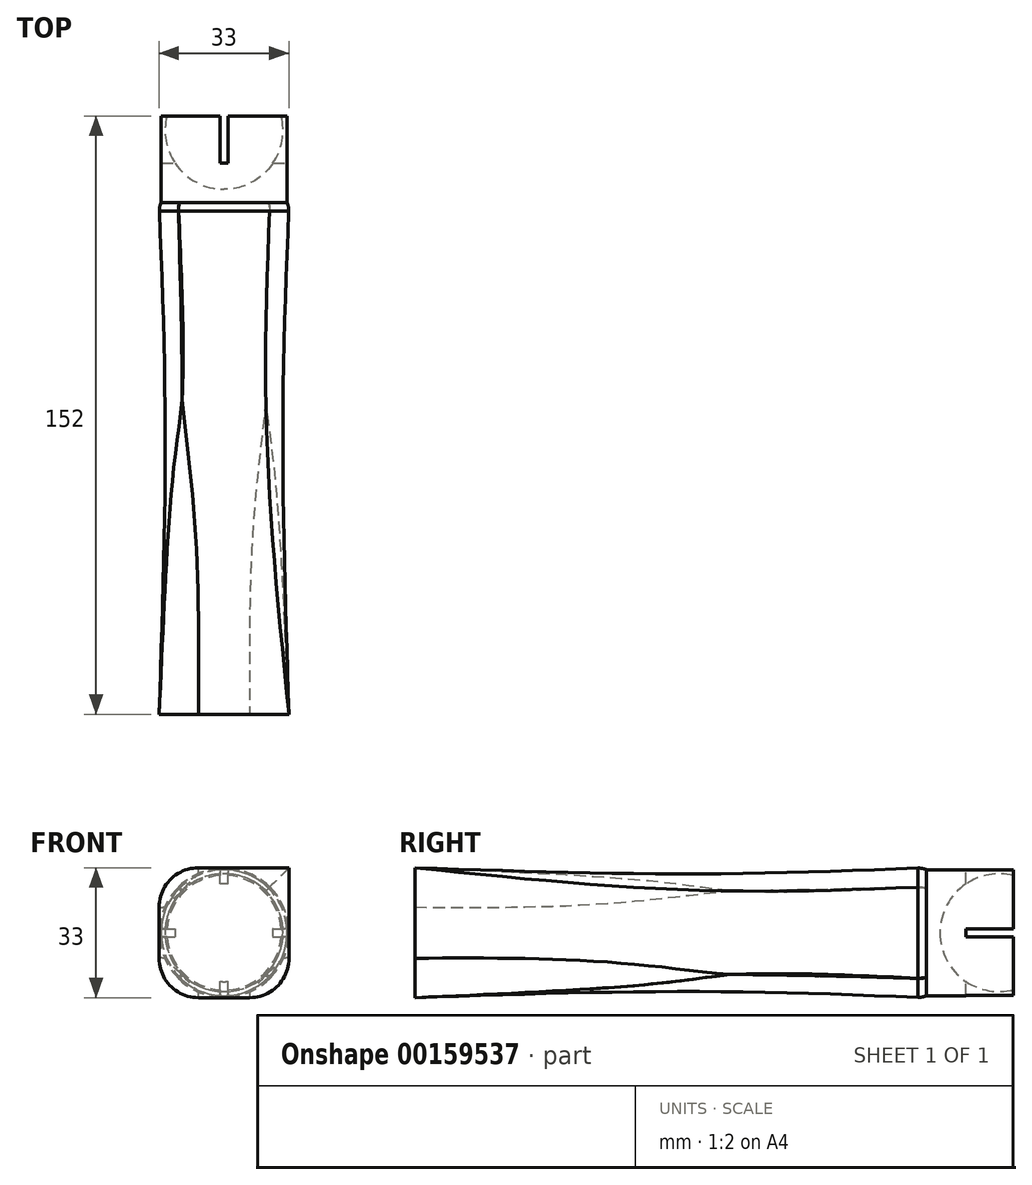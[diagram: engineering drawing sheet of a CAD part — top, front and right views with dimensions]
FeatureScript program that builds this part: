
annotation { "Feature Type Name" : "Feature", "Feature Type Description" : "" }
export const myFeature = defineFeature(function(context is Context, id is Id, definition is map)
    precondition{}
    {
        {
            var Q0;
            Q0=qCreatedBy(makeId("Front.planeOp"),FACE);
            cPlane(context, id + "F0", {"entities" : qUnion([Q0]), "cplaneType" : CPlaneType.OFFSET, "offset" : 70 * mm, "width" : 152.4 * mm, "height" : 152.4 * mm});
        }
        {
            var Q0;
            Q0=qCreatedBy(makeId("Front.planeOp"),FACE);
            cPlane(context, id + "F1", {"entities" : qUnion([Q0]), "cplaneType" : CPlaneType.OFFSET, "offset" : 10 * mm, "oppositeDirection" : true, "width" : 152.4 * mm, "height" : 152.4 * mm});
        }
        {
            var Q0;
            Q0=qCreatedBy(id+"F0.planeOp",FACE);
            var sketch = newSketch(context, id + "F2", { "sketchPlane" : qUnion([Q0])});
            skLineSegment(sketch, "E0.bottom", {"start": v(-16.5, 16.5) * mm, "end": v(16.5, 16.5) * mm});
            skLineSegment(sketch, "E0.top", {"start": v(-16.5, -16.5) * mm, "end": v(16.5, -16.5) * mm});
            skLineSegment(sketch, "E0.left", {"start": v(-16.5, 16.5) * mm, "end": v(-16.5, -16.5) * mm});
            skLineSegment(sketch, "E0.right", {"start": v(16.5, 16.5) * mm, "end": v(16.5, -16.5) * mm});
            skPoint(sketch, "E0.middle", {"position": v(0, 0) * mm});
            skSolve(sketch);
        }
        {
            var Q0;
            Q0=qCreatedBy(id+"F1.planeOp",FACE);
            var sketch = newSketch(context, id + "F3", { "sketchPlane" : qUnion([Q0])});
            skCircle(sketch, "E1", {"center": v(0, 0) * mm, "radius": 15 * mm});
            skSolve(sketch);
        }
        {
            var Q0;
            Q0=qCreatedBy(id+"F1.planeOp",FACE);
            cPlane(context, id + "F4", {"entities" : qUnion([Q0]), "cplaneType" : CPlaneType.OFFSET, "offset" : 50 * mm, "oppositeDirection" : true, "width" : 150 * mm, "height" : 150 * mm});
        }
        {
            var Q0;
            Q0=qCreatedBy(id+"F4.planeOp",FACE);
            var sketch = newSketch(context, id + "F5", { "sketchPlane" : qUnion([Q0])});
            skCircle(sketch, "E2", {"center": v(0, 0) * mm, "radius": 16.5 * mm});
            skSolve(sketch);
        }
        {
            var Q0;
            Q0=makeQuery(id+"F2.imprint","IMPRINT",FACE,{"disambiguationData":[TD([[makeQuery(id+"F2.imprint","IMPRINT",EDGE,{"derivedFrom":sQuery(id+"F2.wireOp",EDGE,"E0.bottom")}),-1.0]])]});
            var Q1;
            Q1=makeQuery(id+"F3.imprint","IMPRINT",FACE,{"disambiguationData":[TD([[makeQuery(id+"F3.imprint","IMPRINT",EDGE,{"derivedFrom":sQuery(id+"F3.wireOp",EDGE,"E1")}),1.0]])]});
            var Q2;
            Q2=makeQuery(id+"F5.imprint","IMPRINT",FACE,{"disambiguationData":[TD([[makeQuery(id+"F5.imprint","IMPRINT",EDGE,{"derivedFrom":sQuery(id+"F5.wireOp",EDGE,"E2")}),1.0]])]});
            loft(context, id + "F6", {"sheetProfilesArray" : [{ "sheetProfileEntities" : qUnion([Q0]) }, { "sheetProfileEntities" : qUnion([Q1]) }, { "sheetProfileEntities" : qUnion([Q2]) }]});
        }
        {
            var Q0;
            Q0=makeQuery(id+"F6.opLoft","SWEPT_EDGE",EDGE,{"disambiguationData":[OSD([sQuery(id+"F2.wireOp",EDGE,"E0.bottom"),sQuery(id+"F2.wireOp",EDGE,"E0.left")]),OD(0.0)]});
            var Q1;
            Q1=makeQuery(id+"F6.opLoft","SWEPT_EDGE",EDGE,{"disambiguationData":[OSD([sQuery(id+"F2.wireOp",EDGE,"E0.bottom"),sQuery(id+"F2.wireOp",EDGE,"E0.left"),sQuery(id+"F2.wireOp",EDGE,"E0.right"),sQuery(id+"F3.wireOp",EDGE,"E1")])]});
            var Q2;
            Q2=makeQuery(id+"F6.opLoft","SWEPT_EDGE",EDGE,{"disambiguationData":[OSD([sQuery(id+"F2.wireOp",EDGE,"E0.top"),sQuery(id+"F2.wireOp",EDGE,"E0.left"),sQuery(id+"F2.wireOp",EDGE,"E0.right"),sQuery(id+"F3.wireOp",EDGE,"E1")])]});
            var Q3;
            Q3=makeQuery(id+"F6.opLoft","SWEPT_EDGE",EDGE,{"disambiguationData":[OSD([sQuery(id+"F2.wireOp",EDGE,"E0.bottom"),sQuery(id+"F2.wireOp",EDGE,"E0.top"),sQuery(id+"F2.wireOp",EDGE,"E0.right"),sQuery(id+"F3.wireOp",EDGE,"E1")])]});
            fillet(context, id + "F7", {"entities" : qUnion([Q0, Q1, Q2, Q3]), "radius" : 10 * mm, "tangentPropagation" : true, "allowEdgeOverflow" : false});
        }
        {
            var Q0;
            Q0=makeQuery(id+"F5.imprint","IMPRINT",FACE,{"disambiguationData":[TD([[makeQuery(id+"F5.imprint","IMPRINT",EDGE,{"derivedFrom":sQuery(id+"F5.wireOp",EDGE,"E2")}),1.0]])]});
            var sketch = newSketch(context, id + "F8", { "sketchPlane" : qUnion([Q0])});
            skCircle(sketch, "E3", {"center": v(0, 0) * mm, "radius": 16 * mm});
            skSolve(sketch);
        }
        {
            var Q0;
            Q0 = qSketchRegion(id + "F8", true);
            extrude(context, id + "F9", {"entities" : qUnion([Q0]), "operationType" : NewBodyOperationType.ADD, "oppositeDirection" : true, "depth" : 22 * mm});
        }
        {
            var Q0;
            Q0=qCreatedBy(makeId("Top.planeOp"),FACE);
            var sketch = newSketch(context, id + "F10", { "sketchPlane" : qUnion([Q0])});
            skArc(sketch, "E4", {"start": v(0, 63.4) * mm, "mid": v(15, 78.4) * mm, "end": v(0, 93.4) * mm});
            skLineSegment(sketch, "E5", {"start": v(0, 224.37) * mm, "end": v(0, 31.68) * mm});
            skSolve(sketch);
        }
        {
            var Q0;
            Q0 = qSketchRegion(id + "F10", true);
            var Q1;
            Q1=sQuery(id+"F10.wireOp",EDGE,"E5");
            revolve(context, id + "F11", {"operationType" : NewBodyOperationType.REMOVE, "entities" : qUnion([Q0]), "axis" : qUnion([Q1]), "revolveType" : RevolveType.FULL, "oppositeDirection" : true});
        }
        {
            var Q0;
            Q0=qCreatedBy(makeId("Top.planeOp"),FACE);
            var sketch = newSketch(context, id + "F12", { "sketchPlane" : qUnion([Q0])});
            skLineSegment(sketch, "E6.bottom", {"start": v(-1, 90) * mm, "end": v(1, 90) * mm});
            skLineSegment(sketch, "E6.top", {"start": v(-1, 70) * mm, "end": v(1, 70) * mm});
            skLineSegment(sketch, "E6.left", {"start": v(-1, 90) * mm, "end": v(-1, 70) * mm});
            skLineSegment(sketch, "E6.right", {"start": v(1, 90) * mm, "end": v(1, 70) * mm});
            skPoint(sketch, "E6.middle", {"position": v(0, 80) * mm});
            skSolve(sketch);
        }
        {
            var Q0;
            Q0 = qSketchRegion(id + "F12", true);
            extrude(context, id + "F13", {"entities" : qUnion([Q0]), "operationType" : NewBodyOperationType.REMOVE, "endBound" : BoundingType.SYMMETRIC, "oppositeDirection" : true, "depth" : 25 * mm});
        }
        {
            var Q0;
            Q0=qCreatedBy(makeId("Right.planeOp"),FACE);
            var sketch = newSketch(context, id + "F14", { "sketchPlane" : qUnion([Q0])});
            skPoint(sketch, "E7.middle", {"position": v(37.45, 0) * mm});
            skLineSegment(sketch, "E8.bottom", {"start": v(90, 1) * mm, "end": v(70, 1) * mm});
            skLineSegment(sketch, "E8.top", {"start": v(90, -1) * mm, "end": v(70, -1) * mm});
            skLineSegment(sketch, "E8.left", {"start": v(90, 1) * mm, "end": v(90, -1) * mm});
            skLineSegment(sketch, "E8.right", {"start": v(70, 1) * mm, "end": v(70, -1) * mm});
            skPoint(sketch, "E8.middle", {"position": v(80, 0) * mm});
            skSolve(sketch);
        }
        {
            var Q0;
            Q0 = qSketchRegion(id + "F12", true);
            extrude(context, id + "F15", {"entities" : qUnion([Q0]), "operationType" : NewBodyOperationType.REMOVE, "endBound" : BoundingType.SYMMETRIC, "oppositeDirection" : true, "depth" : 25 * mm});
        }
        {
            var Q0;
            Q0 = qSketchRegion(id + "F14", true);
            extrude(context, id + "F16", {"entities" : qUnion([Q0]), "operationType" : NewBodyOperationType.REMOVE, "endBound" : BoundingType.SYMMETRIC, "oppositeDirection" : true, "depth" : 25 * mm});
        }
        {
            var Q0;
            Q0 = qSketchRegion(id + "F14", true);
            extrude(context, id + "F17", {"entities" : qUnion([Q0]), "operationType" : NewBodyOperationType.REMOVE, "endBound" : BoundingType.SYMMETRIC, "oppositeDirection" : true, "depth" : 50 * mm});
        }
        {
            var Q0;
            Q0 = qSketchRegion(id + "F12", true);
            extrude(context, id + "F18", {"entities" : qUnion([Q0]), "operationType" : NewBodyOperationType.REMOVE, "endBound" : BoundingType.SYMMETRIC, "oppositeDirection" : true, "depth" : 50 * mm});
        }
        {
            var Q0;
            Q0=makeQuery(id+"F6.opLoft","MID_CAP_EDGE",EDGE,{"disambiguationData":[OSD([sQuery(id+"F2.wireOp",EDGE,"E0.bottom"),sQuery(id+"F2.wireOp",EDGE,"E0.top"),sQuery(id+"F2.wireOp",EDGE,"E0.left"),sQuery(id+"F2.wireOp",EDGE,"E0.right"),sQuery(id+"F5.wireOp",EDGE,"E2")])],"capPos":2.0});
            fillet(context, id + "F19", {"entities" : qUnion([Q0]), "radius" : 5 * mm, "tangentPropagation" : true, "allowEdgeOverflow" : false});
        }
    });
